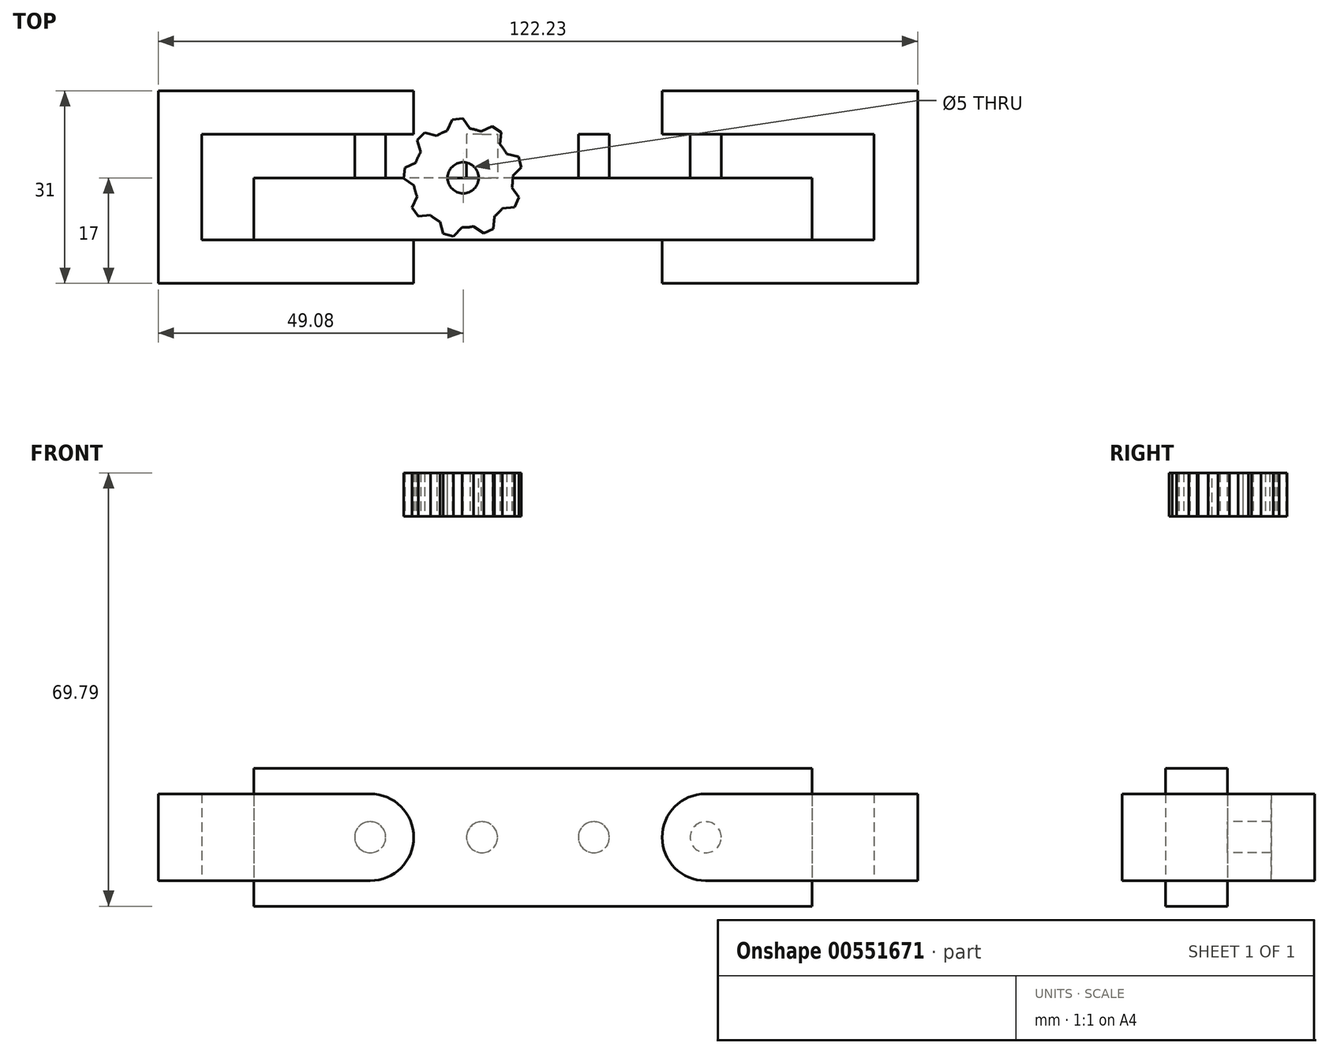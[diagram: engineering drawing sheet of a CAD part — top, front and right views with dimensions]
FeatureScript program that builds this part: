
annotation { "Feature Type Name" : "Feature", "Feature Type Description" : "" }
export const myFeature = defineFeature(function(context is Context, id is Id, definition is map)
    precondition{}
    {
        {
            var Q0;
            Q0=qCreatedBy(makeId("Top.planeOp"),FACE);
            var sketch = newSketch(context, id + "F0", { "sketchPlane" : qUnion([Q0])});
            skCircle(sketch, "E0", {"center": v(-10, 0) * mm, "radius": 8 * mm});
            skCircle(sketch, "E1.cCircle", {"center": v(-10.77, 7.96) * mm, "radius": 1.5 * mm, "construction": true});
            skLineSegment(sketch, "E1.2", {"start": v(-12.49, 7.8) * mm, "end": v(-11.77, 9.37) * mm});
            skLineSegment(sketch, "E1.3", {"start": v(-11.77, 9.37) * mm, "end": v(-10.05, 9.54) * mm});
            skLineSegment(sketch, "E1.4", {"start": v(-10.05, 9.54) * mm, "end": v(-9.04, 8.13) * mm});
            skPoint(sketch, "E1.0.midPoint", {"position": v(-10.62, 6.47) * mm});
            skPoint(sketch, "E2.orphan", {"position": v(-9.76, 6.55) * mm});
            skPoint(sketch, "E3.orphan", {"position": v(-11.48, 6.39) * mm});
            skLineSegment(sketch, "E4", {"start": v(-12.49, 7.8) * mm, "end": v(-12.6, 7.57) * mm});
            skLineSegment(sketch, "E5", {"start": v(-9.04, 8.13) * mm, "end": v(-8.9, 7.92) * mm});
            skLineSegment(sketch, "E6.1.0", {"start": v(-16.17, 7.28) * mm, "end": v(-14.5, 6.84) * mm});
            skLineSegment(sketch, "E6.1.1", {"start": v(-16.92, 4.37) * mm, "end": v(-17.38, 6.04) * mm});
            skLineSegment(sketch, "E6.1.2", {"start": v(-17.38, 6.04) * mm, "end": v(-16.17, 7.28) * mm});
            skLineSegment(sketch, "E6.1.3", {"start": v(-16.92, 4.37) * mm, "end": v(-16.85, 4.13) * mm});
            skLineSegment(sketch, "E6.1.4", {"start": v(-14.5, 6.84) * mm, "end": v(-14.25, 6.78) * mm});
            skLineSegment(sketch, "E6.2.0", {"start": v(-19.4, 1.61) * mm, "end": v(-17.84, 2.36) * mm});
            skLineSegment(sketch, "E6.2.1", {"start": v(-18.11, -1.1) * mm, "end": v(-19.54, -0.12) * mm});
            skLineSegment(sketch, "E6.2.2", {"start": v(-19.54, -0.12) * mm, "end": v(-19.4, 1.61) * mm});
            skLineSegment(sketch, "E6.2.3", {"start": v(-18.11, -1.1) * mm, "end": v(-17.9, -1.24) * mm});
            skLineSegment(sketch, "E6.2.4", {"start": v(-17.84, 2.36) * mm, "end": v(-17.61, 2.46) * mm});
            skLineSegment(sketch, "E7.2.3.0", {"start": v(-18.24, -4.81) * mm, "end": v(-17.52, -3.23) * mm});
            skLineSegment(sketch, "E7.3.3.0", {"start": v(-15.5, -6.05) * mm, "end": v(-17.23, -6.22) * mm});
            skLineSegment(sketch, "E7.6.3.0", {"start": v(-17.23, -6.22) * mm, "end": v(-18.24, -4.81) * mm});
            skLineSegment(sketch, "E7.9.3.0", {"start": v(-15.5, -6.05) * mm, "end": v(-15.26, -6.03) * mm});
            skLineSegment(sketch, "E7.12.3.0", {"start": v(-17.52, -3.23) * mm, "end": v(-17.41, -3) * mm});
            skLineSegment(sketch, "E8.2.4.0", {"start": v(-13.22, -8.98) * mm, "end": v(-13.68, -7.31) * mm});
            skLineSegment(sketch, "E8.3.4.0", {"start": v(-10.33, -8.18) * mm, "end": v(-11.54, -9.41) * mm});
            skLineSegment(sketch, "E8.6.4.0", {"start": v(-11.54, -9.41) * mm, "end": v(-13.22, -8.98) * mm});
            skLineSegment(sketch, "E8.9.4.0", {"start": v(-10.33, -8.18) * mm, "end": v(-10.15, -8) * mm});
            skLineSegment(sketch, "E8.12.4.0", {"start": v(-13.68, -7.31) * mm, "end": v(-13.75, -7.07) * mm});
            skLineSegment(sketch, "E9.2.5.0", {"start": v(-6.7, -8.95) * mm, "end": v(-8.12, -7.97) * mm});
            skLineSegment(sketch, "E9.3.5.0", {"start": v(-5, -6.48) * mm, "end": v(-5.13, -8.2) * mm});
            skLineSegment(sketch, "E9.6.5.0", {"start": v(-5.13, -8.2) * mm, "end": v(-6.7, -8.95) * mm});
            skLineSegment(sketch, "E9.9.5.0", {"start": v(-5, -6.48) * mm, "end": v(-4.97, -6.22) * mm});
            skLineSegment(sketch, "E9.12.5.0", {"start": v(-8.12, -7.97) * mm, "end": v(-8.33, -7.82) * mm});
            skLineSegment(sketch, "E9.2.6.0", {"start": v(-1.72, -4.73) * mm, "end": v(-3.44, -4.9) * mm});
            skLineSegment(sketch, "E9.3.6.0", {"start": v(-2, -1.74) * mm, "end": v(-1, -3.15) * mm});
            skLineSegment(sketch, "E9.6.6.0", {"start": v(-1, -3.15) * mm, "end": v(-1.72, -4.73) * mm});
            skLineSegment(sketch, "E9.9.6.0", {"start": v(-2, -1.74) * mm, "end": v(-2.15, -1.54) * mm});
            skLineSegment(sketch, "E9.12.6.0", {"start": v(-3.44, -4.9) * mm, "end": v(-3.7, -4.92) * mm});
            skLineSegment(sketch, "E10.2.7.0", {"start": v(-0.61, 1.7) * mm, "end": v(-1.83, 0.47) * mm});
            skLineSegment(sketch, "E10.3.7.0", {"start": v(-2.75, 3.8) * mm, "end": v(-1.08, 3.37) * mm});
            skLineSegment(sketch, "E10.6.7.0", {"start": v(-1.08, 3.37) * mm, "end": v(-0.61, 1.7) * mm});
            skLineSegment(sketch, "E10.9.7.0", {"start": v(-2.75, 3.8) * mm, "end": v(-3, 3.87) * mm});
            skLineSegment(sketch, "E10.12.7.0", {"start": v(-1.83, 0.47) * mm, "end": v(-2, 0.29) * mm});
            skLineSegment(sketch, "E11.2.8.0", {"start": v(-3.9, 7.34) * mm, "end": v(-4.04, 5.61) * mm});
            skLineSegment(sketch, "E11.3.8.0", {"start": v(-6.9, 7.57) * mm, "end": v(-5.33, 8.32) * mm});
            skLineSegment(sketch, "E11.6.8.0", {"start": v(-5.33, 8.32) * mm, "end": v(-3.9, 7.34) * mm});
            skLineSegment(sketch, "E11.9.8.0", {"start": v(-6.9, 7.57) * mm, "end": v(-7.12, 7.46) * mm});
            skLineSegment(sketch, "E11.12.8.0", {"start": v(-4.04, 5.61) * mm, "end": v(-4.06, 5.36) * mm});
            skSolve(sketch);
        }
        {
            var Q0;
            Q0=qSketchRegion(id+"F0",true);
            extrude(context, id + "F1", {"entities" : qUnion([Q0]), "depth" : 7 * mm, "offsetDistance" : 25 * mm});
        }
        {
            var Q0;
            Q0=makeQuery(id+"F1.opExtrude","CAP_FACE",FACE,{"disambiguationData":[OSD([sQuery(id+"F0.wireOp",EDGE,"E0"),sQuery(id+"F0.wireOp",EDGE,"E1.2"),sQuery(id+"F0.wireOp",EDGE,"E1.3"),sQuery(id+"F0.wireOp",EDGE,"E1.4"),sQuery(id+"F0.wireOp",EDGE,"E4"),sQuery(id+"F0.wireOp",EDGE,"E5"),sQuery(id+"F0.wireOp",EDGE,"E6.1.0"),sQuery(id+"F0.wireOp",EDGE,"E6.1.1"),sQuery(id+"F0.wireOp",EDGE,"E6.1.2"),sQuery(id+"F0.wireOp",EDGE,"E6.1.3"),sQuery(id+"F0.wireOp",EDGE,"E6.1.4"),sQuery(id+"F0.wireOp",EDGE,"E6.2.0"),sQuery(id+"F0.wireOp",EDGE,"E6.2.1"),sQuery(id+"F0.wireOp",EDGE,"E6.2.2"),sQuery(id+"F0.wireOp",EDGE,"E6.2.3"),sQuery(id+"F0.wireOp",EDGE,"E6.2.4"),sQuery(id+"F0.wireOp",EDGE,"E7.2.3.0"),sQuery(id+"F0.wireOp",EDGE,"E7.3.3.0"),sQuery(id+"F0.wireOp",EDGE,"E7.6.3.0"),sQuery(id+"F0.wireOp",EDGE,"E7.9.3.0"),sQuery(id+"F0.wireOp",EDGE,"E7.12.3.0"),sQuery(id+"F0.wireOp",EDGE,"E8.2.4.0"),sQuery(id+"F0.wireOp",EDGE,"E8.3.4.0"),sQuery(id+"F0.wireOp",EDGE,"E8.6.4.0"),sQuery(id+"F0.wireOp",EDGE,"E8.9.4.0"),sQuery(id+"F0.wireOp",EDGE,"E8.12.4.0"),sQuery(id+"F0.wireOp",EDGE,"E9.2.5.0"),sQuery(id+"F0.wireOp",EDGE,"E9.3.5.0"),sQuery(id+"F0.wireOp",EDGE,"E9.6.5.0"),sQuery(id+"F0.wireOp",EDGE,"E9.9.5.0"),sQuery(id+"F0.wireOp",EDGE,"E9.12.5.0"),sQuery(id+"F0.wireOp",EDGE,"E9.2.6.0"),sQuery(id+"F0.wireOp",EDGE,"E9.3.6.0"),sQuery(id+"F0.wireOp",EDGE,"E9.6.6.0"),sQuery(id+"F0.wireOp",EDGE,"E9.9.6.0"),sQuery(id+"F0.wireOp",EDGE,"E9.12.6.0"),sQuery(id+"F0.wireOp",EDGE,"E10.2.7.0"),sQuery(id+"F0.wireOp",EDGE,"E10.3.7.0"),sQuery(id+"F0.wireOp",EDGE,"E10.6.7.0"),sQuery(id+"F0.wireOp",EDGE,"E10.9.7.0"),sQuery(id+"F0.wireOp",EDGE,"E10.12.7.0"),sQuery(id+"F0.wireOp",EDGE,"E11.2.8.0"),sQuery(id+"F0.wireOp",EDGE,"E11.3.8.0"),sQuery(id+"F0.wireOp",EDGE,"E11.6.8.0"),sQuery(id+"F0.wireOp",EDGE,"E11.9.8.0"),sQuery(id+"F0.wireOp",EDGE,"E11.12.8.0")])],"isStart":false});
            var sketch = newSketch(context, id + "F2", { "sketchPlane" : qUnion([Q0])});
            skCircle(sketch, "E12", {"center": v(-10, 0) * mm, "radius": 2.5 * mm});
            skSolve(sketch);
        }
        {
            var Q0;
            Q0=qSketchRegion(id+"F2",true);
            extrude(context, id + "F3", {"entities" : qUnion([Q0]), "operationType" : NewBodyOperationType.REMOVE, "oppositeDirection" : true, "depth" : 25 * mm, "offsetDistance" : 25 * mm});
        }
        {
            var Q0;
            Q0=qCreatedBy(makeId("Front.planeOp"),FACE);
            var sketch = newSketch(context, id + "F4", { "sketchPlane" : qUnion([Q0])});
            skLineSegment(sketch, "E13.bottom", {"start": v(46.18, -40.6) * mm, "end": v(-43.67, -40.6) * mm});
            skLineSegment(sketch, "E13.top", {"start": v(46.18, -62.79) * mm, "end": v(-43.67, -62.79) * mm});
            skLineSegment(sketch, "E13.left", {"start": v(46.18, -40.6) * mm, "end": v(46.18, -62.79) * mm});
            skLineSegment(sketch, "E13.right", {"start": v(-43.67, -40.6) * mm, "end": v(-43.67, -62.79) * mm});
            skPoint(sketch, "E13.middle", {"position": v(1.26, -51.7) * mm});
            skSolve(sketch);
        }
        {
            var Q0;
            Q0=qSketchRegion(id+"F4",true);
            extrude(context, id + "F5", {"entities" : qUnion([Q0]), "depth" : 10 * mm, "offsetDistance" : 25 * mm});
        }
        {
            var Q0;
            Q0=makeQuery(id+"F5.opExtrude","CAP_FACE",FACE,{"disambiguationData":[OSD([sQuery(id+"F4.wireOp",EDGE,"E13.bottom"),sQuery(id+"F4.wireOp",EDGE,"E13.top"),sQuery(id+"F4.wireOp",EDGE,"E13.left"),sQuery(id+"F4.wireOp",EDGE,"E13.right")])],"isStart":true});
            var sketch = newSketch(context, id + "F6", { "sketchPlane" : qUnion([Q0])});
            skCircle(sketch, "E14", {"center": v(-29.04, -51.7) * mm, "radius": 2.5 * mm});
            skCircle(sketch, "E15.1.0.0", {"center": v(-11.04, -51.7) * mm, "radius": 2.5 * mm});
            skCircle(sketch, "E15.2.0.0", {"center": v(6.96, -51.7) * mm, "radius": 2.5 * mm});
            skCircle(sketch, "E15.3.0.0", {"center": v(24.96, -51.7) * mm, "radius": 2.5 * mm});
            skLineSegment(sketch, "E15.direction1", {"start": v(-29.04, -51.7) * mm, "end": v(-11.04, -51.7) * mm, "construction": true});
            skLineSegment(sketch, "E16", {"start": v(-46.18, -51.7) * mm, "end": v(43.67, -51.7) * mm});
            skSolve(sketch);
        }
        {
            var Q0;
            Q0=makeQuery(id+"F6.imprint","IMPRINT",FACE,{"disambiguationData":[TD([[makeQuery(id+"F6.imprint","IMPRINT",EDGE,{"derivedFrom":sQuery(id+"F6.wireOp",EDGE,"E14")}),1.0]])]});
            var Q1;
            Q1=makeQuery(id+"F6.imprint","IMPRINT",FACE,{"disambiguationData":[TD([[makeQuery(id+"F6.imprint","IMPRINT",EDGE,{"derivedFrom":sQuery(id+"F6.wireOp",EDGE,"E15.1.0.0")}),1.0]])]});
            var Q2;
            Q2=makeQuery(id+"F6.imprint","IMPRINT",FACE,{"disambiguationData":[TD([[makeQuery(id+"F6.imprint","IMPRINT",EDGE,{"derivedFrom":sQuery(id+"F6.wireOp",EDGE,"E15.2.0.0")}),1.0]])]});
            var Q3;
            Q3=makeQuery(id+"F6.imprint","IMPRINT",FACE,{"disambiguationData":[TD([[makeQuery(id+"F6.imprint","IMPRINT",EDGE,{"derivedFrom":sQuery(id+"F6.wireOp",EDGE,"E15.3.0.0")}),1.0]])]});
            extrude(context, id + "F7", {"entities" : qUnion([Q0, Q1, Q2, Q3]), "operationType" : NewBodyOperationType.ADD, "depth" : 7 * mm, "offsetDistance" : 25 * mm});
        }
        {
            var Q0;
            Q0=makeQuery(id+"F5.opExtrude","CAP_FACE",FACE,{"disambiguationData":[OSD([sQuery(id+"F4.wireOp",EDGE,"E13.bottom"),sQuery(id+"F4.wireOp",EDGE,"E13.top"),sQuery(id+"F4.wireOp",EDGE,"E13.left"),sQuery(id+"F4.wireOp",EDGE,"E13.right")])],"isStart":false});
            var sketch = newSketch(context, id + "F8", { "sketchPlane" : qUnion([Q0])});
            skCircle(sketch, "E17", {"center": v(-24.96, -51.7) * mm, "radius": 2.5 * mm});
            skCircle(sketch, "E18", {"center": v(29.04, -51.7) * mm, "radius": 2.5 * mm});
            skSolve(sketch);
        }
        {
            var Q0;
            Q0=qSketchRegion(id+"F8",true);
            extrude(context, id + "F9", {"entities" : qUnion([Q0]), "operationType" : NewBodyOperationType.ADD, "depth" : 7 * mm, "offsetDistance" : 25 * mm});
        }
        {
            var Q0;
            Q0=makeQuery(id+"F9.opExtrude","CAP_FACE",FACE,{"disambiguationData":[OSD([sQuery(id+"F8.wireOp",EDGE,"E17")])],"isStart":false});
            var sketch = newSketch(context, id + "F10", { "sketchPlane" : qUnion([Q0])});
            skCircle(sketch, "E19", {"center": v(-24.96, -51.7) * mm, "radius": 2.5 * mm});
            skCircle(sketch, "E20", {"center": v(-24.96, -51.7) * mm, "radius": 7 * mm});
            skCircle(sketch, "E21", {"center": v(29.04, -51.7) * mm, "radius": 2.5 * mm});
            skCircle(sketch, "E22", {"center": v(29.04, -51.7) * mm, "radius": 7 * mm});
            skLineSegment(sketch, "E23", {"start": v(-24.96, -44.7) * mm, "end": v(-52.08, -44.7) * mm});
            skLineSegment(sketch, "E24", {"start": v(-24.96, -58.7) * mm, "end": v(-52.08, -58.7) * mm});
            skLineSegment(sketch, "E25", {"start": v(29.04, -44.7) * mm, "end": v(56.15, -44.7) * mm});
            skLineSegment(sketch, "E26", {"start": v(29.04, -58.7) * mm, "end": v(56.15, -58.7) * mm});
            skLineSegment(sketch, "E27", {"start": v(-52.08, -44.7) * mm, "end": v(-52.08, -58.7) * mm});
            skLineSegment(sketch, "E28", {"start": v(56.15, -44.7) * mm, "end": v(56.15, -58.7) * mm});
            skSolve(sketch);
        }
        {
            var Q0;
            Q0=qSketchRegion(id+"F10",true);
            extrude(context, id + "F11", {"entities" : qUnion([Q0]), "oppositeDirection" : true, "depth" : 7 * mm, "offsetDistance" : 25 * mm});
        }
        {
            var Q0;
            Q0=makeQuery(id+"F11.opExtrude","SWEPT_FACE",FACE,{"disambiguationData":[OSD([sQuery(id+"F10.wireOp",EDGE,"E27")])]});
            var sketch = newSketch(context, id + "F12", { "sketchPlane" : qUnion([Q0])});
            skLineSegment(sketch, "E29.bottom", {"start": v(17, -58.7) * mm, "end": v(-7, -58.7) * mm});
            skLineSegment(sketch, "E29.top", {"start": v(17, -44.7) * mm, "end": v(-7, -44.7) * mm});
            skLineSegment(sketch, "E29.left", {"start": v(17, -58.7) * mm, "end": v(17, -44.7) * mm});
            skLineSegment(sketch, "E29.right", {"start": v(-7, -58.7) * mm, "end": v(-7, -44.7) * mm});
            skSolve(sketch);
        }
        {
            var Q0;
            Q0=qSketchRegion(id+"F12",true);
            extrude(context, id + "F13", {"entities" : qUnion([Q0]), "operationType" : NewBodyOperationType.ADD, "depth" : 7 * mm, "offsetDistance" : 25 * mm});
        }
        {
            var Q0;
            Q0=makeQuery(id+"F13.opExtrude","SWEPT_FACE",FACE,{"disambiguationData":[OSD([sQuery(id+"F12.wireOp",EDGE,"E29.right")])]});
            var sketch = newSketch(context, id + "F14", { "sketchPlane" : qUnion([Q0])});
            skLineSegment(sketch, "E30.bottom", {"start": v(59.08, -58.7) * mm, "end": v(24.96, -58.7) * mm});
            skLineSegment(sketch, "E30.top", {"start": v(59.08, -44.7) * mm, "end": v(24.96, -44.7) * mm});
            skLineSegment(sketch, "E30.left", {"start": v(59.08, -58.7) * mm, "end": v(59.08, -44.7) * mm});
            skLineSegment(sketch, "E30.right", {"start": v(24.96, -58.7) * mm, "end": v(24.96, -44.7) * mm});
            skArc(sketch, "E31", {"start": v(24.96, -44.7) * mm, "mid": v(17.96, -51.7) * mm, "end": v(24.96, -58.7) * mm});
            skSolve(sketch);
        }
        {
            var Q0;
            Q0=qSketchRegion(id+"F14",true);
            extrude(context, id + "F15", {"entities" : qUnion([Q0]), "operationType" : NewBodyOperationType.ADD, "depth" : 7 * mm, "offsetDistance" : 25 * mm});
        }
        {
            var Q0;
            Q0=makeQuery(id+"F11.opExtrude","SWEPT_FACE",FACE,{"disambiguationData":[OSD([sQuery(id+"F10.wireOp",EDGE,"E28")])]});
            var sketch = newSketch(context, id + "F16", { "sketchPlane" : qUnion([Q0])});
            skLineSegment(sketch, "E32.bottom", {"start": v(-17, -44.7) * mm, "end": v(7, -44.7) * mm});
            skLineSegment(sketch, "E32.top", {"start": v(-17, -58.7) * mm, "end": v(7, -58.7) * mm});
            skLineSegment(sketch, "E32.left", {"start": v(-17, -44.7) * mm, "end": v(-17, -58.7) * mm});
            skLineSegment(sketch, "E32.right", {"start": v(7, -44.7) * mm, "end": v(7, -58.7) * mm});
            skSolve(sketch);
        }
        {
            var Q0;
            Q0=qSketchRegion(id+"F16",true);
            extrude(context, id + "F17", {"entities" : qUnion([Q0]), "operationType" : NewBodyOperationType.ADD, "depth" : 7 * mm, "offsetDistance" : 25 * mm});
        }
        {
            var Q0;
            Q0=makeQuery(id+"F17.opExtrude","SWEPT_FACE",FACE,{"disambiguationData":[OSD([sQuery(id+"F16.wireOp",EDGE,"E32.right")])]});
            var sketch = newSketch(context, id + "F18", { "sketchPlane" : qUnion([Q0])});
            skLineSegment(sketch, "E33.bottom", {"start": v(-63.15, -58.7) * mm, "end": v(-29.04, -58.7) * mm});
            skLineSegment(sketch, "E33.top", {"start": v(-63.15, -44.7) * mm, "end": v(-29.04, -44.7) * mm});
            skLineSegment(sketch, "E33.left", {"start": v(-63.15, -58.7) * mm, "end": v(-63.15, -44.7) * mm});
            skLineSegment(sketch, "E33.right", {"start": v(-29.04, -58.7) * mm, "end": v(-29.04, -44.7) * mm});
            skArc(sketch, "E34", {"start": v(-29.04, -58.7) * mm, "mid": v(-22.04, -51.7) * mm, "end": v(-29.04, -44.7) * mm});
            skSolve(sketch);
        }
        {
            var Q0;
            Q0=qSketchRegion(id+"F18",true);
            extrude(context, id + "F19", {"entities" : qUnion([Q0]), "operationType" : NewBodyOperationType.ADD, "depth" : 7 * mm, "offsetDistance" : 25 * mm});
        }
    });
